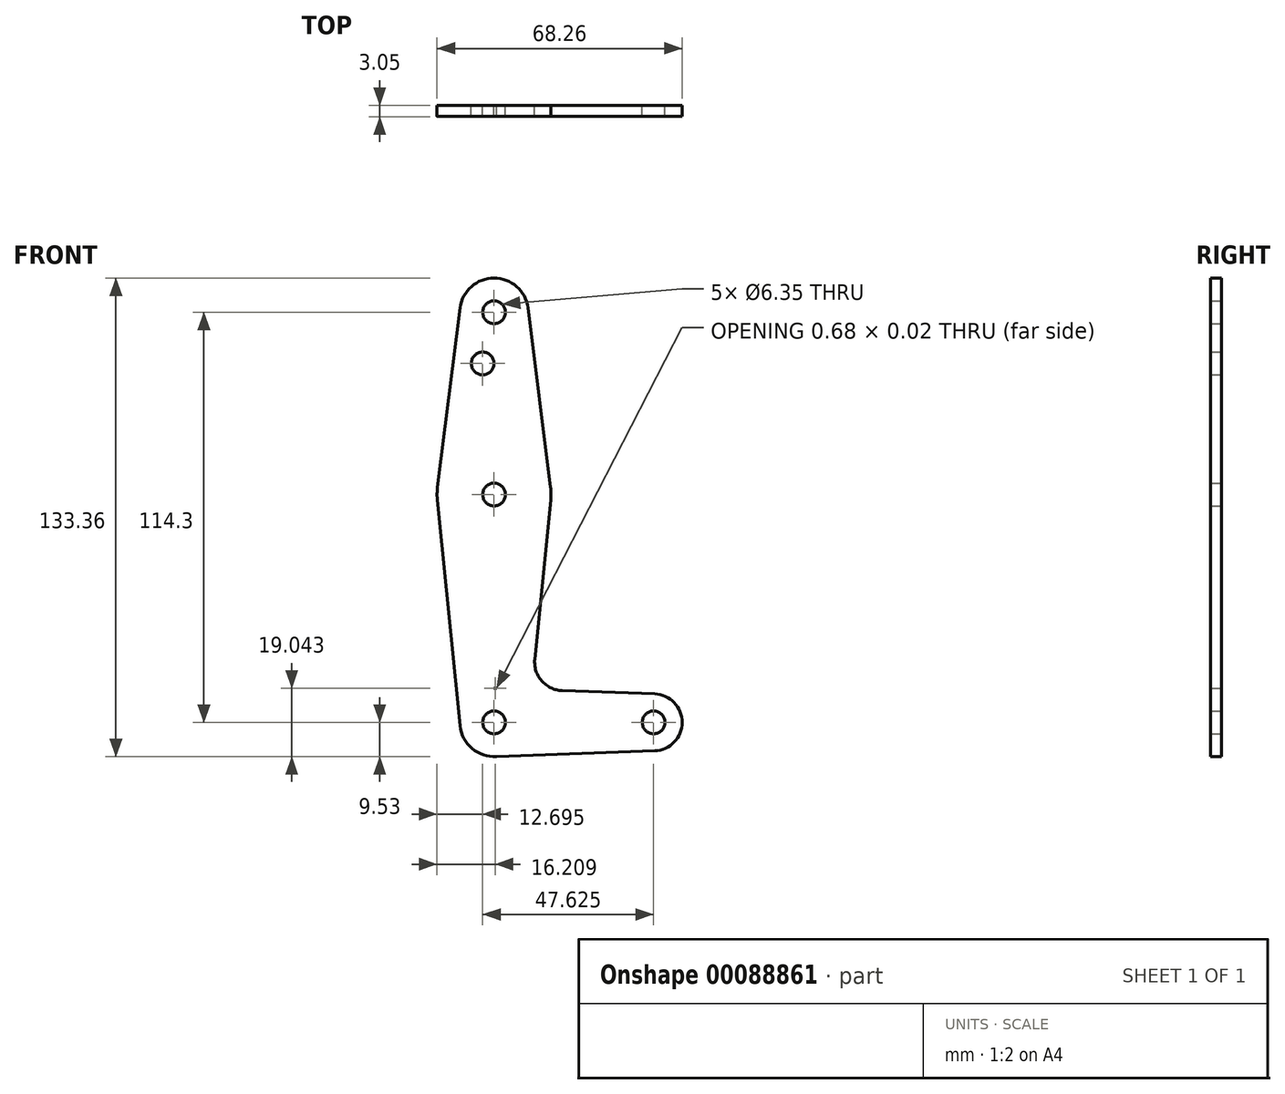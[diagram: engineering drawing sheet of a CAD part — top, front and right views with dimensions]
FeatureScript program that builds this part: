
annotation { "Feature Type Name" : "Feature", "Feature Type Description" : "" }
export const myFeature = defineFeature(function(context is Context, id is Id, definition is map)
    precondition{}
    {
        {
            var Q0;
            Q0=qCreatedBy(makeId("Front.planeOp"),FACE);
            var sketch = newSketch(context, id + "F0", { "sketchPlane" : qUnion([Q0])});
            skCircle(sketch, "E0", {"center": v(0, 114.3) * mm, "radius": 9.53 * mm});
            skLineSegment(sketch, "E1", {"start": v(0, 114.3) * mm, "end": v(0, 63.5) * mm, "construction": true});
            skCircle(sketch, "E2", {"center": v(0, 63.5) * mm, "radius": 15.88 * mm});
            skLineSegment(sketch, "E3", {"start": v(0, 63.5) * mm, "end": v(0, 0) * mm, "construction": true});
            skCircle(sketch, "E4", {"center": v(0, 0) * mm, "radius": 9.53 * mm});
            skLineSegment(sketch, "E5", {"start": v(0, 0) * mm, "end": v(44.45, 0) * mm, "construction": true});
            skCircle(sketch, "E6", {"center": v(44.45, 0) * mm, "radius": 7.94 * mm});
            skLineSegment(sketch, "E7", {"start": v(-9.45, 115.5) * mm, "end": v(-15.75, 65.48) * mm});
            skLineSegment(sketch, "E8", {"start": v(9.45, 115.5) * mm, "end": v(15.75, 65.48) * mm});
            skLineSegment(sketch, "E9", {"start": v(0, 9.53) * mm, "end": v(0.68, 9.5) * mm});
            skLineSegment(sketch, "E10", {"start": v(0, -9.53) * mm, "end": v(44.73, -7.93) * mm});
            skCircle(sketch, "E11", {"center": v(0, 114.3) * mm, "radius": 3.18 * mm});
            skCircle(sketch, "E12", {"center": v(0, 0) * mm, "radius": 3.18 * mm});
            skCircle(sketch, "E13", {"center": v(-3.17, 100.03) * mm, "radius": 3.18 * mm});
            skLineSegment(sketch, "E14", {"start": v(-15.8, 61.91) * mm, "end": v(-9.48, -0.95) * mm});
            skLineSegment(sketch, "E15", {"start": v(15.8, 61.91) * mm, "end": v(11.34, 17.6) * mm});
            skLineSegment(sketch, "E16", {"start": v(18.97, 8.85) * mm, "end": v(44.73, 7.93) * mm});
            skArc(sketch, "E17.filletArc", {"start": v(11.34, 17.6) * mm, "mid": v(13.26, 11.57) * mm, "end": v(18.97, 8.85) * mm});
            skCircle(sketch, "E18", {"center": v(44.45, 0) * mm, "radius": 3.18 * mm});
            skCircle(sketch, "E19", {"center": v(0, 63.5) * mm, "radius": 3.18 * mm});
            skSolve(sketch);
        }
        {
            var Q0;
            Q0 = qSketchRegion(id + "F0", true);
            extrude(context, id + "F1", {"entities" : qUnion([Q0]), "depth" : 3.05 * mm});
        }
    });
